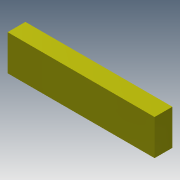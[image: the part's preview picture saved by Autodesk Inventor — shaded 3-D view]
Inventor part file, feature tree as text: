
AUTODESK INVENTOR PART (.ipt)
format: ipt  version: 2013 (Build 170138000, 138)  size: 72,192 bytes
history: native  units: mm
features: extrude x1, sketch x1
ambient origin geometry x8: Origin, YZ Plane, XZ Plane, XY Plane, X Axis, Y Axis, Z Axis, Center Point
bodies: Solid1 (feature_tree)
feature tree (2):
  extrude  "Extrusion1"  Depth=20.0mm
  sketch  "Sketch1"  dims[d0=82.6mm d1=20.0mm d2=10.0mm d3=0.0mm]
